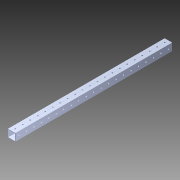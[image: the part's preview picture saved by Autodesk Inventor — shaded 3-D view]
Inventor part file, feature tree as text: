
AUTODESK INVENTOR PART (.ipt)
format: ipt  version: 2014 SP1 (Build 180222100, 222)  size: 1,202,688 bytes
history: native  units: in
note: dims shown in document units (in); Inventor stores cm internally (conversion verified against a paired STEP export)
features: pattern_circular x1, other x1, extrude x1, imported_body x1, sketch x1
ambient origin geometry x8: Origin, YZ Plane, XZ Plane, XY Plane, X Axis, Y Axis, Z Axis, Center Point
bodies: Body1 (feature_tree)
feature tree (5):
  pattern_circular  "CirPattern2"
  other  "1x1 tube1"
  extrude  "Extrusion1"  [1 undecoded]
  imported_body  "Base1"
  sketch  "Sketch1"  dims[d0=38.0in d1=0.0in]
note: 1 required parameter value undecoded (feature->parameter linkage not recoverable at this tier; creation-order binding heuristic only, values carry confidence <= 0.55)
